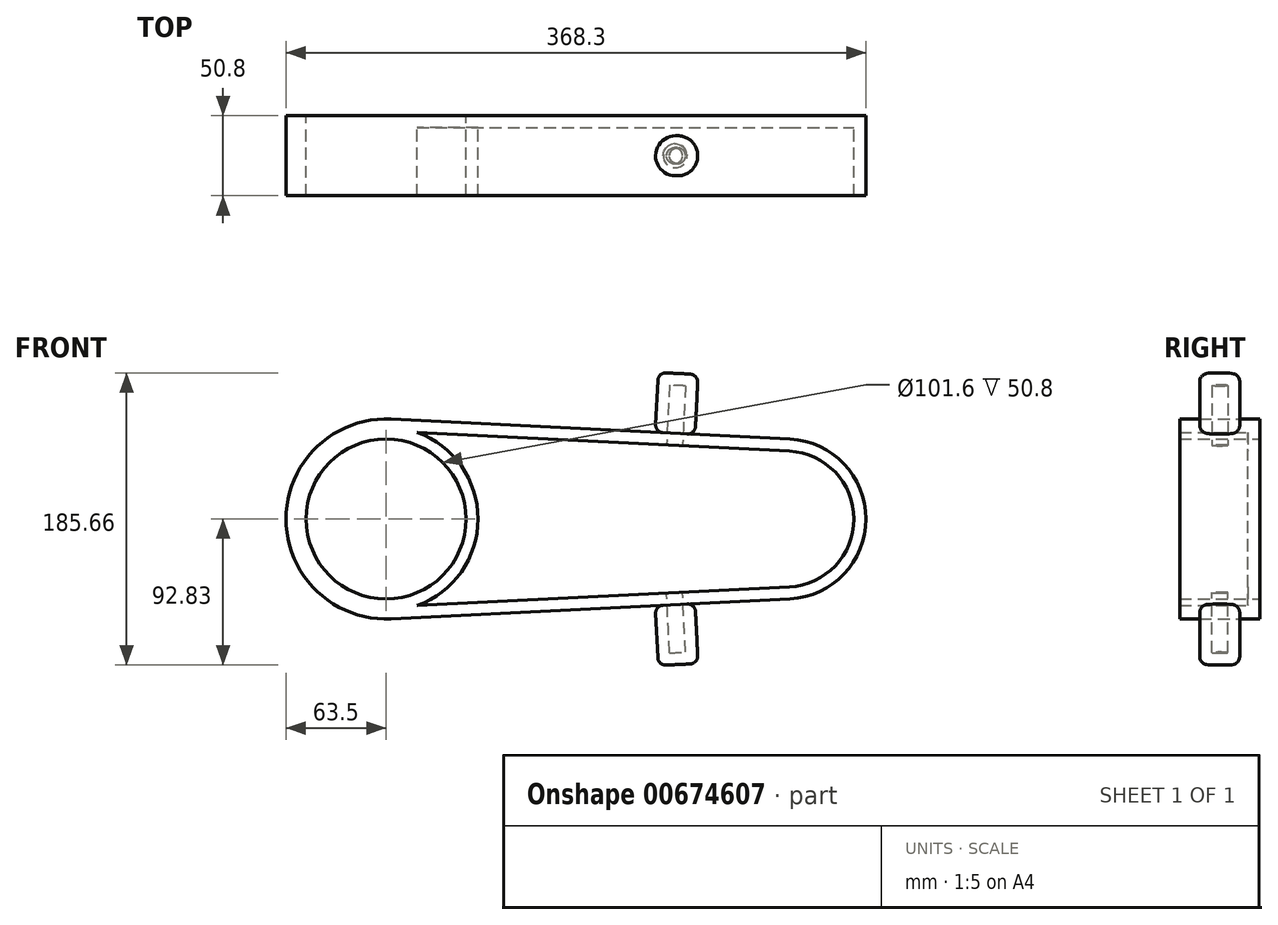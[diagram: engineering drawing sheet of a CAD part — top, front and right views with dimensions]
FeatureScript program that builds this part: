
annotation { "Feature Type Name" : "Feature", "Feature Type Description" : "" }
export const myFeature = defineFeature(function(context is Context, id is Id, definition is map)
    precondition{}
    {
        {
            var Q0;
            Q0=qCreatedBy(makeId("Front.planeOp"),FACE);
            var sketch = newSketch(context, id + "F0", { "sketchPlane" : qUnion([Q0])});
            skCircle(sketch, "E0", {"center": v(0, 0) * mm, "radius": 63.5 * mm});
            skCircle(sketch, "E1", {"center": v(254, 0) * mm, "radius": 50.8 * mm});
            skLineSegment(sketch, "E2", {"start": v(3.17, 63.42) * mm, "end": v(256.54, 50.74) * mm});
            skLineSegment(sketch, "E3", {"start": v(256.54, -50.74) * mm, "end": v(3.17, -63.42) * mm});
            skCircle(sketch, "E4", {"center": v(0, 0) * mm, "radius": 50.8 * mm});
            skSolve(sketch);
        }
        {
            var Q0;
            Q0 = qSketchRegion(id + "F0", true);
            extrude(context, id + "F1", {"entities" : qUnion([Q0]), "depth" : 50.8 * mm, "offsetDistance" : 25.4 * mm});
        }
        {
            var Q0;
            Q0=makeQuery(id+"F1.opExtrude","SWEPT_FACE",FACE,{"disambiguationData":[OSD([sQuery(id+"F0.wireOp",EDGE,"E2")])]});
            var sketch = newSketch(context, id + "F2", { "sketchPlane" : qUnion([Q0])});
            skCircle(sketch, "E5", {"center": v(180.66, -25.4) * mm, "radius": 12.7 * mm});
            skPoint(sketch, "E5.centerSnap0", {"position": v(253.68, -25.4) * mm});
            skSolve(sketch);
        }
        {
            var Q0;
            Q0=makeQuery(id+"F2.imprint","IMPRINT",FACE,{"disambiguationData":[TD([[makeQuery(id+"F2.imprint","IMPRINT",EDGE,{"derivedFrom":sQuery(id+"F2.wireOp",EDGE,"E5")}),1.0]])]});
            extrude(context, id + "F3", {"entities" : qUnion([Q0]), "depth" : 38.1 * mm, "offsetDistance" : 25.4 * mm});
        }
        {
            var Q0;
            Q0=makeQuery(id+"F3.opExtrude","CAP_EDGE",EDGE,{"disambiguationData":[OSD([sQuery(id+"F2.wireOp",EDGE,"E5")])],"isStart":false});
            var Q1;
            Q1=makeQuery(id+"F3.opExtrude","CAP_EDGE",EDGE,{"disambiguationData":[OSD([sQuery(id+"F2.wireOp",EDGE,"E5")])],"isStart":true});
            fillet(context, id + "F4", {"entities" : qUnion([Q0, Q1]), "radius" : 5.08 * mm, "tangentPropagation" : true, "allowEdgeOverflow" : false});
        }
        {
            var Q0;
            Q0=makeQuery(id+"F3.opExtrude","SWEPT_BODY",BODY,{"disambiguationData":[OSD([sQuery(id+"F2.wireOp",EDGE,"E5")])]});
            var Q1;
            Q1=qCreatedBy(makeId("Top.planeOp"),FACE);
            mirror(context, id + "F5", {"operationType" : NewBodyOperationType.ADD, "entities" : qUnion([Q0]), "mirrorPlane" : qUnion([Q1])});
        }
        {
            var Q0;
            Q0=makeQuery(id+"F1.opExtrude","CAP_FACE",FACE,{"disambiguationData":[OSD([sQuery(id+"F0.wireOp",EDGE,"E0"),sQuery(id+"F0.wireOp",EDGE,"E1"),sQuery(id+"F0.wireOp",EDGE,"E2"),sQuery(id+"F0.wireOp",EDGE,"E3"),sQuery(id+"F0.wireOp",EDGE,"E4")])],"isStart":false});
            shell(context, id + "F6", {"entities" : qUnion([Q0]), "thickness" : 7.62 * mm});
        }
    });
